# Revit family: Legrand pre-assembled photovoltaic enclosure
name_source: partatom
category: Equipement électrique
revit_build: Autodesk Revit 2018 (Build: 20170223_1515(x64)
units: mm (PartAtom-declared; Revit-internal decimal feet)

## family parameters
Basée sur le plan de construction = Non
Configuration du panneau = Deux colonnes, circuits au sein
Cote de connecteur circulaire = Utiliser le diamètre
Couper avec des vides une fois chargée = Non
Numéro OmniClass = 23.80.30.11.17
Partagée = Non
Point de calcul de pièce = Non
Titre OmniClass = Distribution Boards and Control Panels
Toujours verticalement = Oui
Type d'élément = Tableau de raccordement

## types (3) — shared parameters
ETIM Class 6.0 = EC000214
Fabricant = Legrand
General Conditions of Use = https://export.legrand.com
IK = 09
IP = 65
Image du type = Plexo3_12_modules_001922_pw_153883_pz_0.jpg
Material = Polystyrene
Polystyrene
RAL = 7046
URL = www.legrand.fr

## per-type parameters (varying)
| type | Cabinet 414001 | Cabinet 414003 | Cabinet 414020 | Cable with MC4 type connector (downstream connection) | Part AC | Part DC | Photovoltaic signalling kit | Protected lightning protection | circuit breaker | connector type MC4 | differential switch | switch-disconnector |
| Legrand enclosure pre-equipped 3kWc DC 414003 | Non | Oui | Non |  | Non | Oui | Oui |  |  | connexion |  | 25A 600V |
| Legrand enclosure pre-equipped 3kWc DC + AC 414001 | Oui | Non | Non | downstream connector | Oui | Oui | Oui | type 2 - 12kA (0 039 51) | DNX³ 4.5kA 20A curve C | connexion | 30 mA type F (ex Hpi) | 25A 600V |
| Legrand enclosure pre-equipped AC 220V 414020 | Non | Non | Oui |  | Oui | Non | Non | type 2 - 12kA (0 039 51) | DNX³ 4.5kA 20A curve C |  | 30 mA type F (ex Hpi) |  |

note: column(s) folded — value = type name in every type: Description
